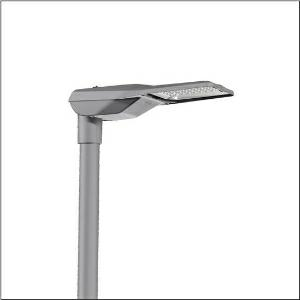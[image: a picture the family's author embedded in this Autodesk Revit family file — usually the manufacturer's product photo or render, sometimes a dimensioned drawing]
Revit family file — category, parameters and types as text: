
# Revit family: streetlight_sl_21_mini___st0_5a_5xe2b43s08jb_3299
name_source: partatom
category: Lighting Fixtures
units: mm (PartAtom-declared; Revit-internal decimal feet)

## family parameters
Cut with Voids When Loaded = No
Host = Face
Light Source = No
Part Type = Normal
Room Calculation Point = No
Round Connector Dimension = Use Diameter
Shared = No

## types (1)
- --- (1 x LED, 13500 lm, 88.6 W, 4000K)
    Apparent Load = 89 VA
    CIE Flux Codes = 43 76 97 100 100
    Color Rendering = 70
    Color Temperature = 4000K
    Default Elevation = 1800 mm
    Description = Streetlight SL 21 mini, mast luminaire, primary light control with lens, of PMMA, primary optical cover: cover, of toughened safety glass, transparent, light distribution: ST0.5a, light emission: direct distribution, primary light characteristic: asymmetric, installation type: side-entry, post-top, LED, High Power LED, rated luminous flux: 13.500lm, luminous efficacy: 152lm/W, light colour: 740, colour temperature: 4000K, control gear: D4i, control: overheat protection, constant luminous flux control, time-dependent luminous flux control, flexible luminous flux parameterisation, pre-setting: logarithmic dimming characteristic, mains connection: 220..240V, AC, 50/60Hz, start of lifetime: 89W, end of service life: 92W, reduction: 41W, luminaire housing, of diecast aluminium, powder-coated, SITECO metallic grey (DB 702S), corrosivity category C5 high according to DIN EN ISO 12944, please order mast flange separately, inclination adjustable: 0°, 5°, 10°, 15°, sealing non-destructively replaceable, multi-level sealing system, length: 628mm, width: 235mm, height: 110mm, mast flange for spigot size: 42mm (side-entry): 5XC10008XM4, 60/48mm (side-entry/post-top): 5XC10108XM2, 76/60mm (side-entry/post-top): 5XC10108XM1, mounting height: 4..8m, Smart Interface above, protection rating (complete): IP66, insulation class (complete): insulation class II (safety insulation), certification: CE, ENEC, ENEC+, VDE, impact resistance: IK10, permissible operating ambient temperature for outdoor applications: -40..+50°C, standard-compliant lighting for roads and squares, packaging unit: 1 piece

Light Distribution: ST0.5a
    Height = 110 mm
    Lamp = 1 x LED
    Lamp Light Flux = 13500 lm
    Lamp Power = 88.6 W
    Lamp count = 1
    Length = 625 mm
    Luminous efficacy = 152 lm/W
    Manufacturer = Siteco
    ModVariant = No
    Model = 5XE2B43S08JB
    Number of Poles = 1
    OnlyDefault = Yes
    Power Factor = 1
    Product Name = Streetlight SL 21 mini | ST0.5a
    Product group = mast luminaire | pylon top
    ProductGroupID = 6100
    Protection Class = Protection class II
    Protection Degree = IP 66
    RLX_Detail_Level = 1
    RLX_Emergency_Light_Flux = 0 lm
    RLX_Emergency_Type = 0
    RLX_Emergency_Type_DB = No
    RlxData = <blob elided: 37365 chars, md5=4a82d340>
    Socket = socket
    Standby Power = 0 W
    System Light Flux = 13500 lm
    System Power = 89 W
    Type Comments = factory setting: luminous flux: 100 % | dim-lin: 254 | 915 mA
    Type Image = l_1003515.jpg
    URL = http://relux.com
    VarID = @adj_032033
    Voltage = 0 V
    Weight = 0.00 kg
    Width = 234 mm

## geometry (parser evidence)
native form markers: Blend x4, Sweep x11
no freeform markers — native parametric forms only
